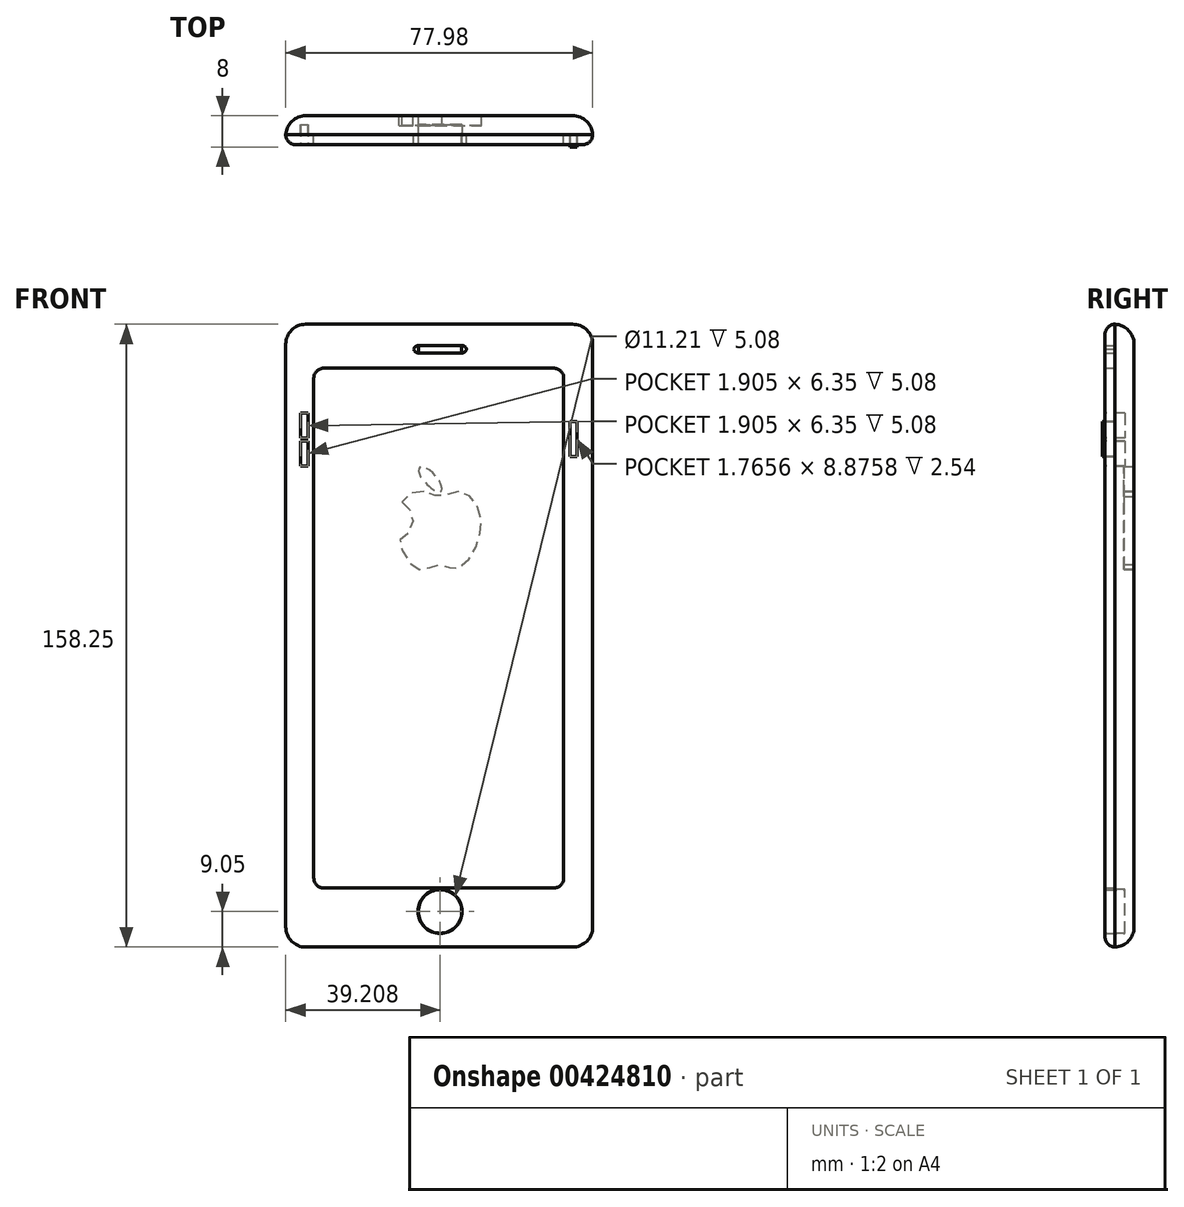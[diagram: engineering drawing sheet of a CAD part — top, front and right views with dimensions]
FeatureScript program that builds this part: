
annotation { "Feature Type Name" : "Feature", "Feature Type Description" : "" }
export const myFeature = defineFeature(function(context is Context, id is Id, definition is map)
    precondition{}
    {
        {
            var Q0;
            Q0=qCreatedBy(makeId("Front.planeOp"),FACE);
            var sketch = newSketch(context, id + "F0", { "sketchPlane" : qUnion([Q0])});
            skLineSegment(sketch, "E0.bottom", {"start": v(-52.37, 93.79) * mm, "end": v(25.6, 93.79) * mm});
            skLineSegment(sketch, "E0.top", {"start": v(-52.37, -64.46) * mm, "end": v(25.6, -64.46) * mm});
            skLineSegment(sketch, "E0.left", {"start": v(-52.37, 93.79) * mm, "end": v(-52.37, -64.46) * mm});
            skLineSegment(sketch, "E0.right", {"start": v(25.6, 93.79) * mm, "end": v(25.6, -64.46) * mm});
            skSolve(sketch);
        }
        {
            var Q0;
            Q0=makeQuery(id+"F0.imprint","IMPRINT",FACE,{"disambiguationData":[TD([[makeQuery(id+"F0.imprint","IMPRINT",EDGE,{"derivedFrom":sQuery(id+"F0.wireOp",EDGE,"E0.bottom")}),-1.0]])]});
            extrude(context, id + "F1", {"entities" : qUnion([Q0]), "depth" : 7.37 * mm});
        }
        {
            var Q0;
            Q0=makeQuery(id+"F1.opExtrude","SWEPT_EDGE",EDGE,{"disambiguationData":[OSD([sQuery(id+"F0.wireOp",EDGE,"E0.top"),sQuery(id+"F0.wireOp",EDGE,"E0.right")])]});
            var Q1;
            Q1=makeQuery(id+"F1.opExtrude","SWEPT_EDGE",EDGE,{"disambiguationData":[OSD([sQuery(id+"F0.wireOp",EDGE,"E0.top"),sQuery(id+"F0.wireOp",EDGE,"E0.left")])]});
            fillet(context, id + "F2", {"entities" : qUnion([Q0, Q1]), "radius" : 5.08 * mm, "tangentPropagation" : true, "allowEdgeOverflow" : false});
        }
        {
            var Q0;
            Q0=makeQuery(id+"F1.opExtrude","SWEPT_EDGE",EDGE,{"disambiguationData":[OSD([sQuery(id+"F0.wireOp",EDGE,"E0.bottom"),sQuery(id+"F0.wireOp",EDGE,"E0.right")])]});
            var Q1;
            Q1=makeQuery(id+"F1.opExtrude","SWEPT_EDGE",EDGE,{"disambiguationData":[OSD([sQuery(id+"F0.wireOp",EDGE,"E0.bottom"),sQuery(id+"F0.wireOp",EDGE,"E0.left")])]});
            fillet(context, id + "F3", {"entities" : qUnion([Q0, Q1]), "radius" : 5.08 * mm, "tangentPropagation" : true, "allowEdgeOverflow" : false});
        }
        {
            var Q0;
            Q0=makeQuery(id+"F1.opExtrude","CAP_EDGE",EDGE,{"disambiguationData":[OSD([sQuery(id+"F0.wireOp",EDGE,"E0.bottom")])],"isStart":false});
            var Q1;
            Q1=makeQuery(id+"F1.opExtrude","CAP_EDGE",EDGE,{"disambiguationData":[OSD([sQuery(id+"F0.wireOp",EDGE,"E0.right")])],"isStart":false});
            var Q2;
            Q2=makeQuery(id+"F1.opExtrude","CAP_EDGE",EDGE,{"disambiguationData":[OSD([sQuery(id+"F0.wireOp",EDGE,"E0.left")])],"isStart":false});
            var Q3;
            Q3=makeQuery(id+"F1.opExtrude","CAP_EDGE",EDGE,{"disambiguationData":[OSD([sQuery(id+"F0.wireOp",EDGE,"E0.top")])],"isStart":false});
            fillet(context, id + "F4", {"entities" : qUnion([Q0, Q1, Q2, Q3]), "radius" : 2.54 * mm, "tangentPropagation" : true, "allowEdgeOverflow" : false});
        }
        {
            var Q0;
            Q0=makeQuery(id+"F1.opExtrude","CAP_EDGE",EDGE,{"disambiguationData":[OSD([sQuery(id+"F0.wireOp",EDGE,"E0.bottom")])],"isStart":true});
            var Q1;
            Q1=makeQuery(id+"F1.opExtrude","CAP_EDGE",EDGE,{"disambiguationData":[OSD([sQuery(id+"F0.wireOp",EDGE,"E0.right")])],"isStart":true});
            var Q2;
            Q2=makeQuery(id+"F1.opExtrude","CAP_EDGE",EDGE,{"disambiguationData":[OSD([sQuery(id+"F0.wireOp",EDGE,"E0.left")])],"isStart":true});
            var Q3;
            Q3=makeQuery(id+"F1.opExtrude","CAP_EDGE",EDGE,{"disambiguationData":[OSD([sQuery(id+"F0.wireOp",EDGE,"E0.top")])],"isStart":true});
            fillet(context, id + "F5", {"entities" : qUnion([Q0, Q1, Q2, Q3]), "radius" : 5.08 * mm, "tangentPropagation" : true, "allowEdgeOverflow" : false});
        }
        {
            var Q0;
            Q0=makeQuery(id+"F1.opExtrude","CAP_FACE",FACE,{"disambiguationData":[OSD([sQuery(id+"F0.wireOp",EDGE,"E0.bottom"),sQuery(id+"F0.wireOp",EDGE,"E0.top"),sQuery(id+"F0.wireOp",EDGE,"E0.left"),sQuery(id+"F0.wireOp",EDGE,"E0.right")])],"isStart":false});
            var sketch = newSketch(context, id + "F6", { "sketchPlane" : qUnion([Q0])});
            skLineSegment(sketch, "E1.bottom", {"start": v(-45.25, 82.62) * mm, "end": v(18.25, 82.62) * mm});
            skLineSegment(sketch, "E1.top", {"start": v(-45.25, -49.46) * mm, "end": v(18.25, -49.46) * mm});
            skLineSegment(sketch, "E1.left", {"start": v(-45.25, 82.62) * mm, "end": v(-45.25, -49.46) * mm});
            skLineSegment(sketch, "E1.right", {"start": v(18.25, 82.62) * mm, "end": v(18.25, -49.46) * mm});
            skSolve(sketch);
        }
        {
            var Q0;
            Q0=makeQuery(id+"F6.imprint","IMPRINT",FACE,{"disambiguationData":[TD([[makeQuery(id+"F6.imprint","IMPRINT",EDGE,{"derivedFrom":sQuery(id+"F6.wireOp",EDGE,"E1.bottom")}),-1.0]])]});
            extrude(context, id + "F7", {"entities" : qUnion([Q0]), "operationType" : NewBodyOperationType.REMOVE, "oppositeDirection" : true, "depth" : 2.54 * mm});
        }
        {
            var Q0;
            Q0=makeQuery(id+"F7.boolean.opBoolean","COPY",EDGE,{"derivedFrom":makeQuery(id+"F7.opExtrude","SWEPT_EDGE",EDGE,{"disambiguationData":[OSD([sQuery(id+"F6.wireOp",EDGE,"E1.bottom"),sQuery(id+"F6.wireOp",EDGE,"E1.right")])]})});
            fillet(context, id + "F8", {"entities" : qUnion([Q0]), "radius" : 2.54 * mm, "tangentPropagation" : true, "allowEdgeOverflow" : false});
        }
        {
            var Q0;
            Q0=makeQuery(id+"F7.boolean.opBoolean","COPY",EDGE,{"derivedFrom":makeQuery(id+"F7.opExtrude","SWEPT_EDGE",EDGE,{"disambiguationData":[OSD([sQuery(id+"F6.wireOp",EDGE,"E1.bottom"),sQuery(id+"F6.wireOp",EDGE,"E1.left")])]})});
            fillet(context, id + "F9", {"entities" : qUnion([Q0]), "radius" : 2.54 * mm, "tangentPropagation" : true, "allowEdgeOverflow" : false});
        }
        {
            var Q0;
            Q0=makeQuery(id+"F7.boolean.opBoolean","COPY",EDGE,{"derivedFrom":makeQuery(id+"F7.opExtrude","SWEPT_EDGE",EDGE,{"disambiguationData":[OSD([sQuery(id+"F6.wireOp",EDGE,"E1.top"),sQuery(id+"F6.wireOp",EDGE,"E1.left")])]})});
            fillet(context, id + "F10", {"entities" : qUnion([Q0]), "radius" : 2.54 * mm, "tangentPropagation" : true, "allowEdgeOverflow" : false});
        }
        {
            var Q0;
            Q0=makeQuery(id+"F7.boolean.opBoolean","COPY",EDGE,{"derivedFrom":makeQuery(id+"F7.opExtrude","SWEPT_EDGE",EDGE,{"disambiguationData":[OSD([sQuery(id+"F6.wireOp",EDGE,"E1.top"),sQuery(id+"F6.wireOp",EDGE,"E1.right")])]})});
            fillet(context, id + "F11", {"entities" : qUnion([Q0]), "radius" : 2.54 * mm, "tangentPropagation" : true, "allowEdgeOverflow" : false});
        }
        {
            var Q0;
            Q0=makeQuery(id+"F7.boolean.opBoolean","COPY",FACE,{"derivedFrom":makeQuery(id+"F7.opExtrude","CAP_FACE",FACE,{"disambiguationData":[OSD([sQuery(id+"F6.wireOp",EDGE,"E1.bottom"),sQuery(id+"F6.wireOp",EDGE,"E1.top"),sQuery(id+"F6.wireOp",EDGE,"E1.left"),sQuery(id+"F6.wireOp",EDGE,"E1.right")])],"isStart":false})});
            var sketch = newSketch(context, id + "F12", { "sketchPlane" : qUnion([Q0])});
            skSolve(sketch);
        }
        {
            var Q0;
            {var subQ3=sQuery(id+"F6.wireOp",EDGE,"E1.bottom");Q0=makeQuery(id+"F12.imprint","IMPRINT",FACE,{"disambiguationData":[TD([[makeQuery(id+"F12.imprint","IMPRINT",EDGE,{"derivedFrom":makeQuery(id+"F7.boolean.opBoolean","COPY",EDGE,{"derivedFrom":makeQuery(id+"F7.opExtrude","CAP_EDGE",EDGE,{"disambiguationData":[OSD([subQ3])],"isStart":false})})}),-1.0]])]});}
            extrude(context, id + "F13", {"entities" : qUnion([Q0]), "depth" : 2.54 * mm});
        }
        {
            var Q0;
            Q0=makeQuery(id+"F1.opExtrude","CAP_FACE",FACE,{"disambiguationData":[OSD([sQuery(id+"F0.wireOp",EDGE,"E0.bottom"),sQuery(id+"F0.wireOp",EDGE,"E0.top"),sQuery(id+"F0.wireOp",EDGE,"E0.left"),sQuery(id+"F0.wireOp",EDGE,"E0.right")])],"isStart":false});
            var sketch = newSketch(context, id + "F14", { "sketchPlane" : qUnion([Q0])});
            skCircle(sketch, "E2", {"center": v(-13.16, -55.41) * mm, "radius": 5.6 * mm});
            skSolve(sketch);
        }
        {
            var Q0;
            Q0=makeQuery(id+"F14.imprint","IMPRINT",FACE,{"disambiguationData":[TD([[makeQuery(id+"F14.imprint","IMPRINT",EDGE,{"derivedFrom":sQuery(id+"F14.wireOp",EDGE,"E2")}),1.0]])]});
            extrude(context, id + "F15", {"entities" : qUnion([Q0]), "operationType" : NewBodyOperationType.REMOVE, "oppositeDirection" : true, "depth" : 5.08 * mm});
        }
        {
            var Q0;
            Q0=makeQuery(id+"F15.boolean.opBoolean","COPY",FACE,{"derivedFrom":makeQuery(id+"F15.opExtrude","CAP_FACE",FACE,{"disambiguationData":[OSD([sQuery(id+"F14.wireOp",EDGE,"E2")])],"isStart":false})});
            var sketch = newSketch(context, id + "F16", { "sketchPlane" : qUnion([Q0])});
            skCircle(sketch, "E3", {"center": v(-13.16, -55.41) * mm, "radius": 5.52 * mm});
            skSolve(sketch);
        }
        {
            var Q0;
            Q0 = qSketchRegion(id + "F16", true);
            extrude(context, id + "F17", {"entities" : qUnion([Q0]), "depth" : 5.08 * mm});
        }
        {
            var Q0;
            Q0=makeQuery(id+"F1.opExtrude","CAP_FACE",FACE,{"disambiguationData":[OSD([sQuery(id+"F0.wireOp",EDGE,"E0.bottom"),sQuery(id+"F0.wireOp",EDGE,"E0.top"),sQuery(id+"F0.wireOp",EDGE,"E0.left"),sQuery(id+"F0.wireOp",EDGE,"E0.right")])],"isStart":false});
            var sketch = newSketch(context, id + "F18", { "sketchPlane" : qUnion([Q0])});
            skLineSegment(sketch, "E4.bottom", {"start": v(-19.9, 86.48) * mm, "end": v(-6.42, 86.48) * mm});
            skLineSegment(sketch, "E4.top", {"start": v(-19.9, 88.4) * mm, "end": v(-6.42, 88.4) * mm});
            skLineSegment(sketch, "E4.left", {"start": v(-19.9, 86.48) * mm, "end": v(-19.9, 88.4) * mm});
            skLineSegment(sketch, "E4.right", {"start": v(-6.42, 86.48) * mm, "end": v(-6.42, 88.4) * mm});
            skSolve(sketch);
        }
        {
            var Q0;
            Q0 = qSketchRegion(id + "F18", true);
            extrude(context, id + "F19", {"entities" : qUnion([Q0]), "operationType" : NewBodyOperationType.REMOVE, "oppositeDirection" : true, "depth" : 2.54 * mm});
        }
        {
            var Q0;
            Q0=makeQuery(id+"F19.boolean.opBoolean","COPY",EDGE,{"derivedFrom":makeQuery(id+"F19.opExtrude","SWEPT_EDGE",EDGE,{"disambiguationData":[OSD([sQuery(id+"F18.wireOp",EDGE,"E4.top"),sQuery(id+"F18.wireOp",EDGE,"E4.right")])]})});
            var Q1;
            Q1=makeQuery(id+"F19.boolean.opBoolean","COPY",EDGE,{"derivedFrom":makeQuery(id+"F19.opExtrude","SWEPT_EDGE",EDGE,{"disambiguationData":[OSD([sQuery(id+"F18.wireOp",EDGE,"E4.bottom"),sQuery(id+"F18.wireOp",EDGE,"E4.left")])]})});
            var Q2;
            Q2=makeQuery(id+"F19.boolean.opBoolean","COPY",EDGE,{"derivedFrom":makeQuery(id+"F19.opExtrude","SWEPT_EDGE",EDGE,{"disambiguationData":[OSD([sQuery(id+"F18.wireOp",EDGE,"E4.bottom"),sQuery(id+"F18.wireOp",EDGE,"E4.right")])]})});
            var Q3;
            Q3=makeQuery(id+"F19.boolean.opBoolean","COPY",EDGE,{"derivedFrom":makeQuery(id+"F19.opExtrude","SWEPT_EDGE",EDGE,{"disambiguationData":[OSD([sQuery(id+"F18.wireOp",EDGE,"E4.top"),sQuery(id+"F18.wireOp",EDGE,"E4.left")])]})});
            fillet(context, id + "F20", {"entities" : qUnion([Q0, Q1, Q2, Q3]), "radius" : 1.27 * mm, "tangentPropagation" : true, "allowEdgeOverflow" : false});
        }
        {
            var Q0;
            Q0=makeQuery(id+"F19.boolean.opBoolean","COPY",FACE,{"derivedFrom":makeQuery(id+"F19.opExtrude","CAP_FACE",FACE,{"disambiguationData":[OSD([sQuery(id+"F18.wireOp",EDGE,"E4.bottom"),sQuery(id+"F18.wireOp",EDGE,"E4.top"),sQuery(id+"F18.wireOp",EDGE,"E4.left"),sQuery(id+"F18.wireOp",EDGE,"E4.right")])],"isStart":false})});
            var sketch = newSketch(context, id + "F21", { "sketchPlane" : qUnion([Q0])});
            skLineSegment(sketch, "E5.bottom", {"start": v(-18.63, 86.48) * mm, "end": v(-7.7, 86.48) * mm});
            skLineSegment(sketch, "E5.top", {"start": v(-18.63, 88.4) * mm, "end": v(-7.7, 88.4) * mm});
            skLineSegment(sketch, "E5.left", {"start": v(-18.63, 86.48) * mm, "end": v(-18.63, 88.4) * mm});
            skLineSegment(sketch, "E5.right", {"start": v(-7.7, 86.48) * mm, "end": v(-7.7, 88.4) * mm});
            skSolve(sketch);
        }
        {
            var Q0;
            Q0 = qSketchRegion(id + "F21", true);
            extrude(context, id + "F22", {"entities" : qUnion([Q0]), "depth" : 2.54 * mm});
        }
        {
            var Q0;
            Q0=makeQuery(id+"F1.opExtrude","CAP_FACE",FACE,{"disambiguationData":[OSD([sQuery(id+"F0.wireOp",EDGE,"E0.bottom"),sQuery(id+"F0.wireOp",EDGE,"E0.top"),sQuery(id+"F0.wireOp",EDGE,"E0.left"),sQuery(id+"F0.wireOp",EDGE,"E0.right")])],"isStart":false});
            var sketch = newSketch(context, id + "F23", { "sketchPlane" : qUnion([Q0])});
            skLineSegment(sketch, "E6.bottom", {"start": v(-48.56, 71.2) * mm, "end": v(-46.65, 71.2) * mm});
            skLineSegment(sketch, "E6.top", {"start": v(-48.56, 64.86) * mm, "end": v(-46.65, 64.86) * mm});
            skLineSegment(sketch, "E6.left", {"start": v(-48.56, 71.2) * mm, "end": v(-48.56, 64.86) * mm});
            skLineSegment(sketch, "E6.right", {"start": v(-46.65, 71.2) * mm, "end": v(-46.65, 64.86) * mm});
            skLineSegment(sketch, "E7.bottom", {"start": v(-48.6, 64.12) * mm, "end": v(-46.7, 64.12) * mm});
            skLineSegment(sketch, "E7.top", {"start": v(-48.6, 57.77) * mm, "end": v(-46.7, 57.77) * mm});
            skLineSegment(sketch, "E7.left", {"start": v(-48.6, 64.12) * mm, "end": v(-48.6, 57.77) * mm});
            skLineSegment(sketch, "E7.right", {"start": v(-46.7, 64.12) * mm, "end": v(-46.7, 57.77) * mm});
            skSolve(sketch);
        }
        {
            var Q0;
            Q0 = qSketchRegion(id + "F23", true);
            extrude(context, id + "F24", {"entities" : qUnion([Q0]), "operationType" : NewBodyOperationType.REMOVE, "oppositeDirection" : true, "depth" : 5.08 * mm});
        }
        {
            var Q0;
            Q0=makeQuery(id+"F24.boolean.opBoolean","COPY",FACE,{"derivedFrom":makeQuery(id+"F24.opExtrude","CAP_FACE",FACE,{"disambiguationData":[OSD([sQuery(id+"F23.wireOp",EDGE,"E6.bottom"),sQuery(id+"F23.wireOp",EDGE,"E6.top"),sQuery(id+"F23.wireOp",EDGE,"E6.left"),sQuery(id+"F23.wireOp",EDGE,"E6.right")])],"isStart":false})});
            var sketch = newSketch(context, id + "F25", { "sketchPlane" : qUnion([Q0])});
            skLineSegment(sketch, "E8.bottom", {"start": v(-48.56, 71.2) * mm, "end": v(-46.65, 71.2) * mm});
            skLineSegment(sketch, "E8.top", {"start": v(-48.56, 64.86) * mm, "end": v(-46.65, 64.86) * mm});
            skLineSegment(sketch, "E8.left", {"start": v(-48.56, 71.2) * mm, "end": v(-48.56, 64.86) * mm});
            skLineSegment(sketch, "E8.right", {"start": v(-46.65, 71.2) * mm, "end": v(-46.65, 64.86) * mm});
            skSolve(sketch);
        }
        {
            var Q0;
            Q0 = qSketchRegion(id + "F25", true);
            extrude(context, id + "F26", {"entities" : qUnion([Q0]), "depth" : 5.08 * mm});
        }
        {
            var Q0;
            Q0=makeQuery(id+"F24.boolean.opBoolean","COPY",FACE,{"derivedFrom":makeQuery(id+"F24.opExtrude","CAP_FACE",FACE,{"disambiguationData":[OSD([sQuery(id+"F23.wireOp",EDGE,"E7.bottom"),sQuery(id+"F23.wireOp",EDGE,"E7.top"),sQuery(id+"F23.wireOp",EDGE,"E7.left"),sQuery(id+"F23.wireOp",EDGE,"E7.right")])],"isStart":false})});
            var sketch = newSketch(context, id + "F27", { "sketchPlane" : qUnion([Q0])});
            skLineSegment(sketch, "E9.bottom", {"start": v(-48.6, 64.12) * mm, "end": v(-46.7, 64.12) * mm});
            skLineSegment(sketch, "E9.top", {"start": v(-48.6, 57.77) * mm, "end": v(-46.7, 57.77) * mm});
            skLineSegment(sketch, "E9.left", {"start": v(-48.6, 64.12) * mm, "end": v(-48.6, 57.77) * mm});
            skLineSegment(sketch, "E9.right", {"start": v(-46.7, 64.12) * mm, "end": v(-46.7, 57.77) * mm});
            skSolve(sketch);
        }
        {
            var Q0;
            Q0 = qSketchRegion(id + "F27", true);
            extrude(context, id + "F28", {"entities" : qUnion([Q0]), "depth" : 2.54 * mm});
        }
        {
            var Q0;
            Q0=makeQuery(id+"F1.opExtrude","CAP_FACE",FACE,{"disambiguationData":[OSD([sQuery(id+"F0.wireOp",EDGE,"E0.bottom"),sQuery(id+"F0.wireOp",EDGE,"E0.top"),sQuery(id+"F0.wireOp",EDGE,"E0.left"),sQuery(id+"F0.wireOp",EDGE,"E0.right")])],"isStart":false});
            var sketch = newSketch(context, id + "F29", { "sketchPlane" : qUnion([Q0])});
            skLineSegment(sketch, "E10", {"start": v(19.85, 69.04) * mm, "end": v(19.85, 60.16) * mm});
            skLineSegment(sketch, "E11", {"start": v(19.85, 60.16) * mm, "end": v(21.61, 60.16) * mm});
            skLineSegment(sketch, "E12", {"start": v(21.61, 60.16) * mm, "end": v(21.61, 69.04) * mm});
            skLineSegment(sketch, "E13", {"start": v(19.85, 69.04) * mm, "end": v(21.61, 69.04) * mm});
            skSolve(sketch);
        }
        {
            var Q0;
            Q0=makeQuery(id+"F29.imprint","IMPRINT",FACE,{"disambiguationData":[TD([[makeQuery(id+"F29.imprint","IMPRINT",EDGE,{"derivedFrom":sQuery(id+"F29.wireOp",EDGE,"E10")}),1.0]])]});
            var Q1;
            Q1=sQuery(id+"F29.wireOp",EDGE,"E10");
            var Q2;
            Q2=sQuery(id+"F29.wireOp",EDGE,"E13");
            var Q3;
            Q3=sQuery(id+"F29.wireOp",EDGE,"E12");
            var Q4;
            Q4=sQuery(id+"F29.wireOp",EDGE,"E11");
            extrude(context, id + "F30", {"entities" : qUnion([Q0]), "operationType" : NewBodyOperationType.REMOVE, "surfaceEntities" : qUnion([Q1, Q2, Q3, Q4]), "oppositeDirection" : true, "depth" : 2.54 * mm});
        }
        {
            var Q0;
            Q0=makeQuery(id+"F30.boolean.opBoolean","COPY",FACE,{"derivedFrom":makeQuery(id+"F30.opExtrude","CAP_FACE",FACE,{"disambiguationData":[OSD([sQuery(id+"F29.wireOp",EDGE,"E10"),sQuery(id+"F29.wireOp",EDGE,"E11"),sQuery(id+"F29.wireOp",EDGE,"E12"),sQuery(id+"F29.wireOp",EDGE,"E13")])],"isStart":false})});
            var sketch = newSketch(context, id + "F31", { "sketchPlane" : qUnion([Q0])});
            skLineSegment(sketch, "E14.bottom", {"start": v(19.85, 69.04) * mm, "end": v(21.61, 69.04) * mm});
            skLineSegment(sketch, "E14.top", {"start": v(19.85, 60.16) * mm, "end": v(21.61, 60.16) * mm});
            skLineSegment(sketch, "E14.left", {"start": v(19.85, 69.04) * mm, "end": v(19.85, 60.16) * mm});
            skLineSegment(sketch, "E14.right", {"start": v(21.61, 69.04) * mm, "end": v(21.61, 60.16) * mm});
            skSolve(sketch);
        }
        {
            var Q0;
            Q0 = qSketchRegion(id + "F31", true);
            extrude(context, id + "F32", {"entities" : qUnion([Q0]), "depth" : 3.17 * mm});
        }
        {
            var Q0;
            Q0=makeQuery(id+"F1.opExtrude","CAP_FACE",FACE,{"disambiguationData":[OSD([sQuery(id+"F0.wireOp",EDGE,"E0.bottom"),sQuery(id+"F0.wireOp",EDGE,"E0.top"),sQuery(id+"F0.wireOp",EDGE,"E0.left"),sQuery(id+"F0.wireOp",EDGE,"E0.right")])],"isStart":true});
            var sketch = newSketch(context, id + "F33", { "sketchPlane" : qUnion([Q0])});
            skFitSpline(sketch, "E15", {"points": [v(18.25, 57.57) * mm, v(18.36, 55.53) * mm, v(17, 53.71) * mm, v(15.52, 52.24) * mm, v(12.91, 51.33) * mm, v(14.05, 54.96) * mm, v(18.25, 57.57) * mm]});
            skFitSpline(sketch, "E16", {"points": [v(22.79, 48.6) * mm, v(20.86, 46.68) * mm, v(20.18, 43.16) * mm, v(22.22, 39.64) * mm, v(23.58, 38.5) * mm, v(21.08, 33.62) * mm, v(19.04, 31.7) * mm, v(16.32, 31.7) * mm, v(14.28, 32.6) * mm, v(11.44, 32.37) * mm, v(9.62, 31.58) * mm, v(6.22, 33.62) * mm, v(3.83, 37.7) * mm, v(2.7, 42.82) * mm, v(3.38, 46.79) * mm, v(5.88, 50.3) * mm, v(9.28, 51.22) * mm, v(13.14, 49.97) * mm, v(15.98, 50.87) * mm, v(19.84, 51.22) * mm, v(22.79, 48.6) * mm]});
            skSolve(sketch);
        }
        {
            var Q0;
            Q0 = qSketchRegion(id + "F33", true);
            extrude(context, id + "F34", {"entities" : qUnion([Q0]), "oppositeDirection" : true, "depth" : 2.54 * mm});
        }
    });
